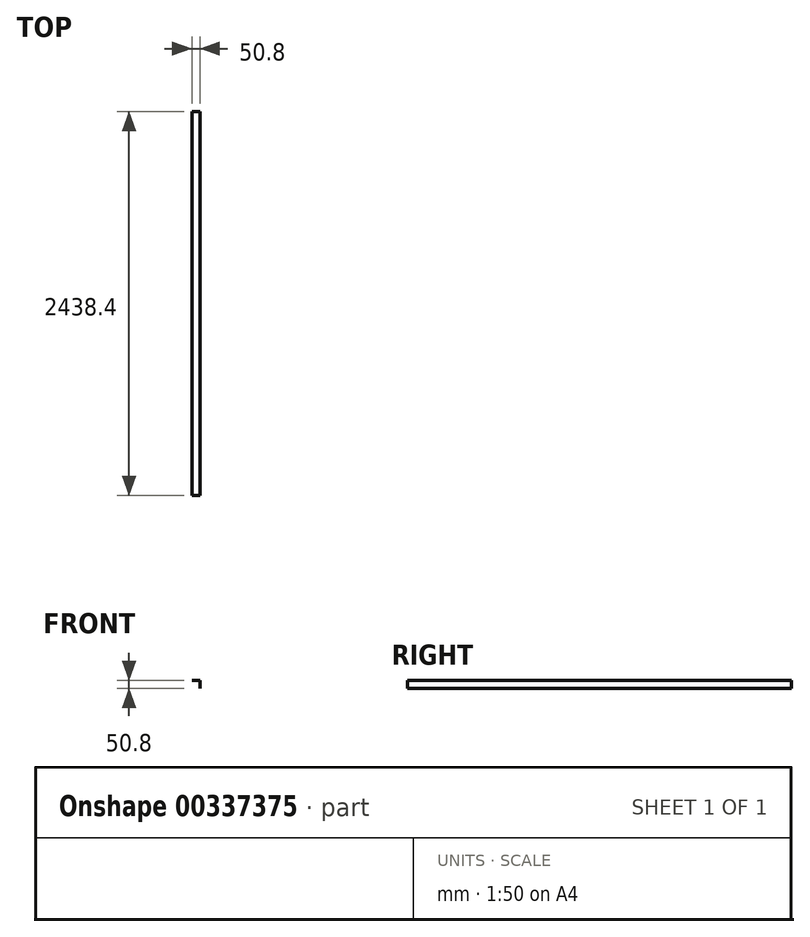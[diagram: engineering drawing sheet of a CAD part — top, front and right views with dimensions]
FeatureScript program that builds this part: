
annotation { "Feature Type Name" : "Feature", "Feature Type Description" : "" }
export const myFeature = defineFeature(function(context is Context, id is Id, definition is map)
    precondition{}
    {
        {
            var Q0;
            Q0=qCreatedBy(makeId("Front.planeOp"),FACE);
            var sketch = newSketch(context, id + "F0", { "sketchPlane" : qUnion([Q0])});
            skLineSegment(sketch, "E0", {"start": v(-55.18, 29.8) * mm, "end": v(-4.38, 29.8) * mm});
            skLineSegment(sketch, "E1", {"start": v(-4.38, 29.8) * mm, "end": v(-4.38, -21) * mm});
            skSolve(sketch);
        }
        {
            var Q0;
            Q0 = qSketchRegion(id + "F0", true);
            var Q1;
            Q1=sQuery(id+"F0.wireOp",EDGE,"E0");
            var Q2;
            Q2=sQuery(id+"F0.wireOp",EDGE,"E1");
            extrude(context, id + "F1", {"entities" : qUnion([Q0]), "bodyType" : ToolBodyType.SURFACE, "surfaceEntities" : qUnion([Q1, Q2]), "depth" : 2438.4 * mm});
        }
    });
